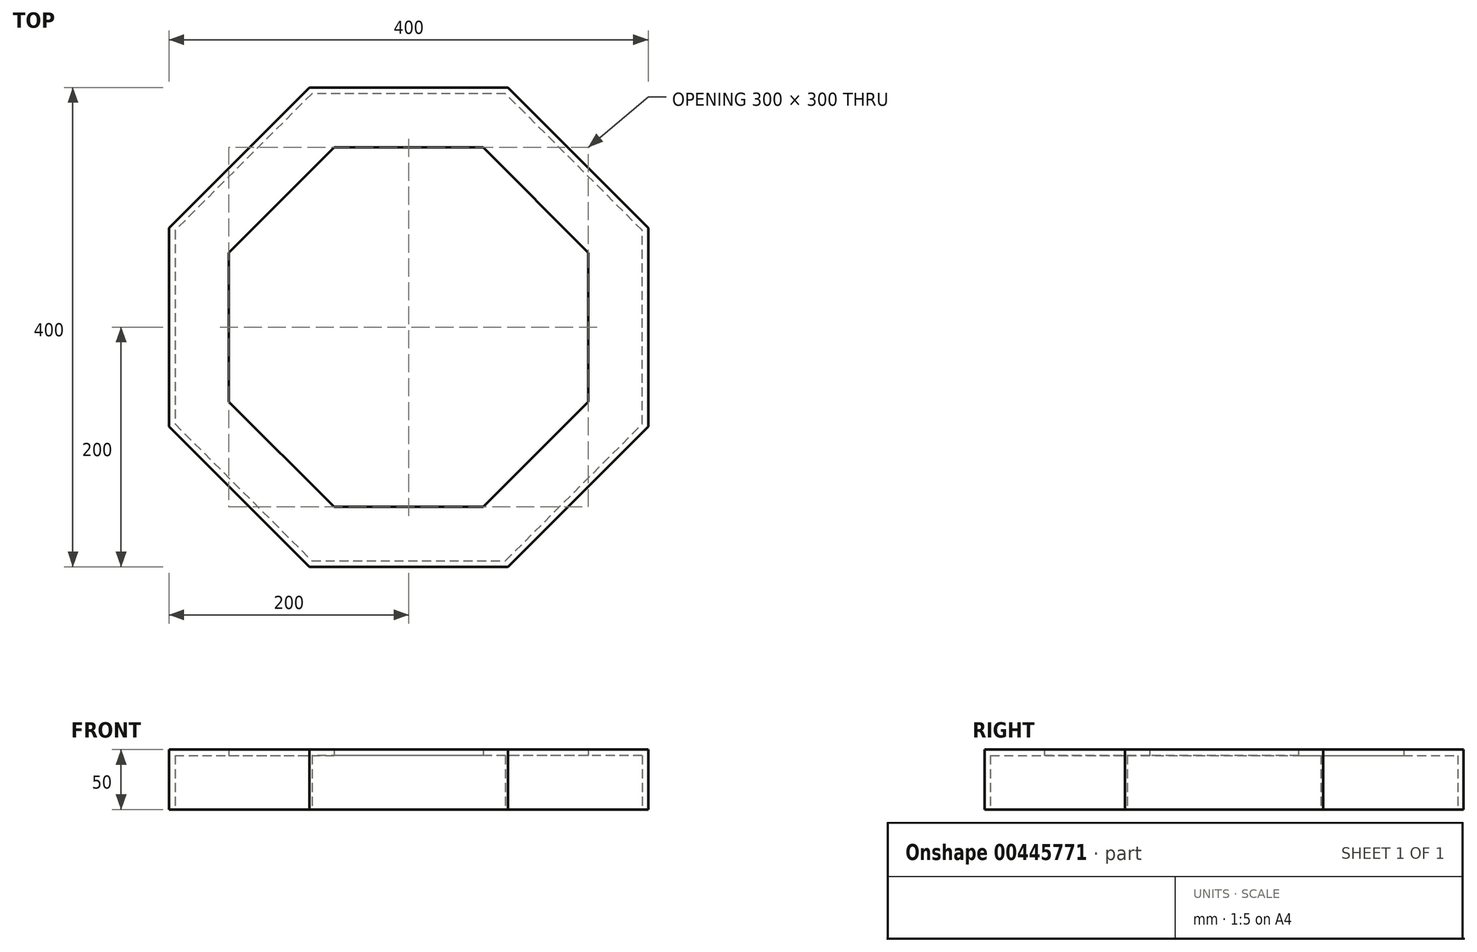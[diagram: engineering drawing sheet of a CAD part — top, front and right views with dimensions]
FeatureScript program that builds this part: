
annotation { "Feature Type Name" : "Feature", "Feature Type Description" : "" }
export const myFeature = defineFeature(function(context is Context, id is Id, definition is map)
    precondition{}
    {
        {
            var Q0;
            Q0=qCreatedBy(makeId("Top.planeOp"),FACE);
            var sketch = newSketch(context, id + "F0", { "sketchPlane" : qUnion([Q0])});
            skCircle(sketch, "E0.cCircle", {"center": v(0, 0) * mm, "radius": 200 * mm, "construction": true});
            skLineSegment(sketch, "E0.0", {"start": v(200, 82.84) * mm, "end": v(200, -82.84) * mm});
            skLineSegment(sketch, "E0.1", {"start": v(200, -82.84) * mm, "end": v(82.84, -200) * mm});
            skLineSegment(sketch, "E0.2", {"start": v(82.84, -200) * mm, "end": v(-82.84, -200) * mm});
            skLineSegment(sketch, "E0.3", {"start": v(-82.84, -200) * mm, "end": v(-200, -82.84) * mm});
            skLineSegment(sketch, "E0.4", {"start": v(-200, -82.84) * mm, "end": v(-200, 82.84) * mm});
            skLineSegment(sketch, "E0.5", {"start": v(-200, 82.84) * mm, "end": v(-82.84, 200) * mm});
            skLineSegment(sketch, "E0.6", {"start": v(-82.84, 200) * mm, "end": v(82.84, 200) * mm});
            skLineSegment(sketch, "E0.7", {"start": v(82.84, 200) * mm, "end": v(200, 82.84) * mm});
            skPoint(sketch, "E0.0.midPoint", {"position": v(200, 0) * mm});
            skSolve(sketch);
        }
        {
            var Q0;
            Q0=qCreatedBy(makeId("Front.planeOp"),FACE);
            var sketch = newSketch(context, id + "F1", { "sketchPlane" : qUnion([Q0])});
            skLineSegment(sketch, "E1", {"start": v(-200, 0) * mm, "end": v(-150, 0) * mm});
            skLineSegment(sketch, "E2", {"start": v(-150, 0) * mm, "end": v(-150, -5) * mm});
            skLineSegment(sketch, "E3", {"start": v(-150, -5) * mm, "end": v(-195, -5) * mm});
            skLineSegment(sketch, "E4", {"start": v(-195, -5) * mm, "end": v(-195, -50) * mm});
            skLineSegment(sketch, "E5", {"start": v(-195, -50) * mm, "end": v(-200, -50) * mm});
            skLineSegment(sketch, "E6", {"start": v(-200, -50) * mm, "end": v(-200, 0) * mm});
            skSolve(sketch);
        }
        {
            var Q0;
            Q0=makeQuery(id+"F1.imprint","IMPRINT",FACE,{"disambiguationData":[TD([[makeQuery(id+"F1.imprint","IMPRINT",EDGE,{"derivedFrom":sQuery(id+"F1.wireOp",EDGE,"E1")}),-1.0]])]});
            var Q1;
            Q1=sQuery(id+"F0.wireOp",EDGE,"E0.4");
            var Q2;
            Q2=sQuery(id+"F0.wireOp",EDGE,"E0.5");
            var Q3;
            Q3=sQuery(id+"F0.wireOp",EDGE,"E0.6");
            var Q4;
            Q4=sQuery(id+"F0.wireOp",EDGE,"E0.7");
            var Q5;
            Q5=sQuery(id+"F0.wireOp",EDGE,"E0.0");
            var Q6;
            Q6=sQuery(id+"F0.wireOp",EDGE,"E0.1");
            var Q7;
            Q7=sQuery(id+"F0.wireOp",EDGE,"E0.2");
            var Q8;
            Q8=sQuery(id+"F0.wireOp",EDGE,"E0.3");
            sweep(context, id + "F2", {"profiles" : qUnion([Q0]), "path" : qUnion([Q1, Q2, Q3, Q4, Q5, Q6, Q7, Q8])});
        }
    });
